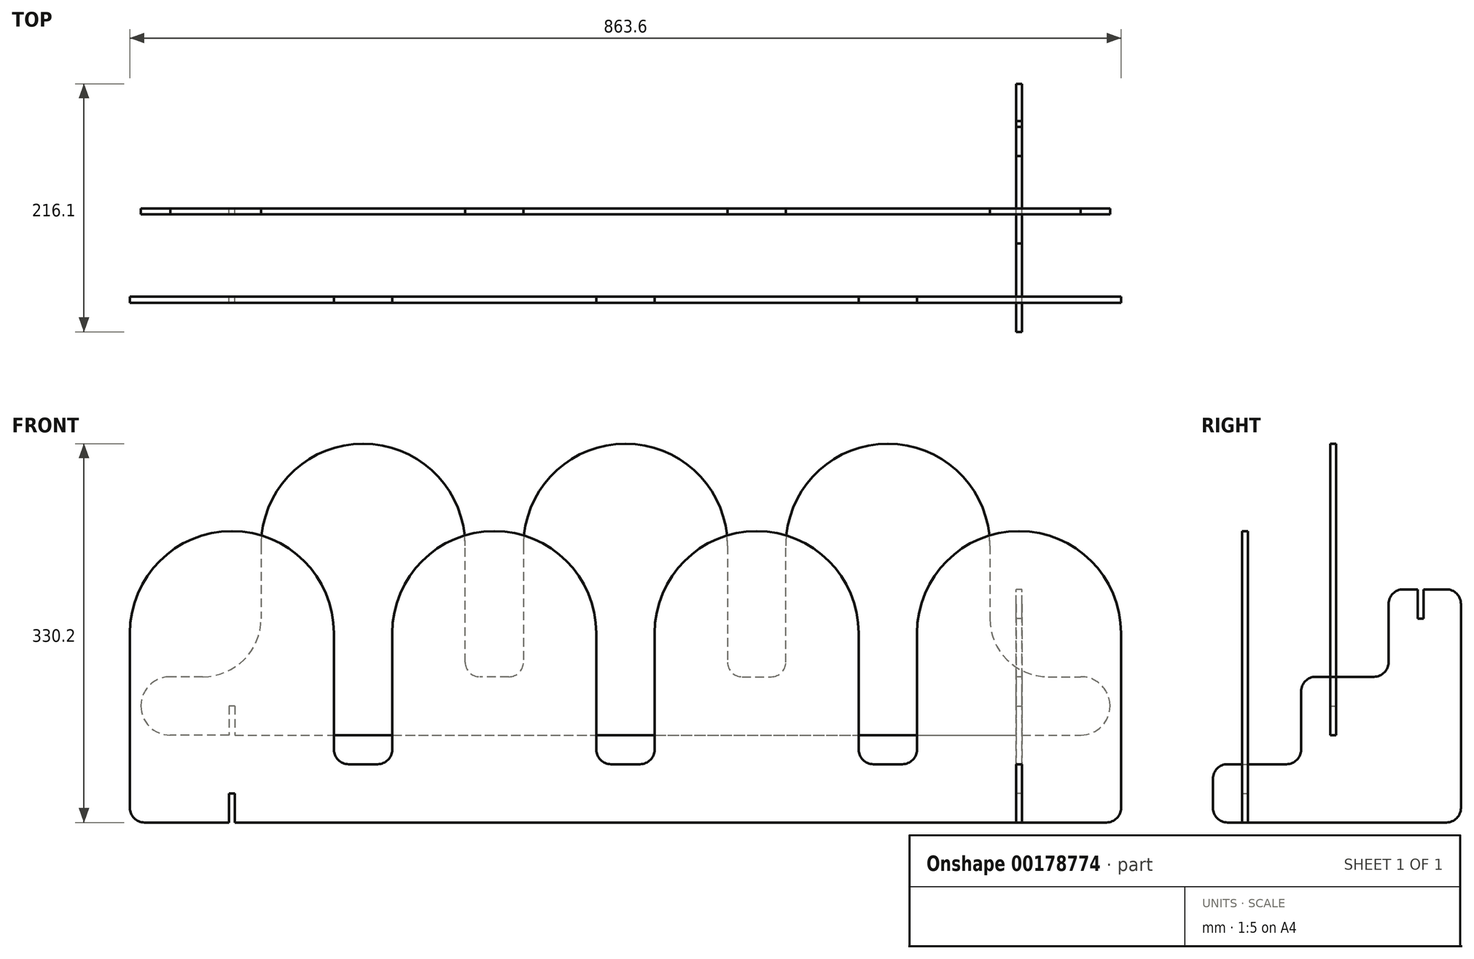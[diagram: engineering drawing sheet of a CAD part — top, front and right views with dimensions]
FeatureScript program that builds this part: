
annotation { "Feature Type Name" : "Feature", "Feature Type Description" : "" }
export const myFeature = defineFeature(function(context is Context, id is Id, definition is map)
    precondition{}
    {
        {
            var Q0;
            Q0=qCreatedBy(makeId("Front.planeOp"),FACE);
            var sketch = newSketch(context, id + "F0", { "sketchPlane" : qUnion([Q0])});
            skLineSegment(sketch, "E0", {"start": v(0, 0) * mm, "end": v(419.1, 0) * mm});
            skLineSegment(sketch, "E1", {"start": v(431.8, 12.7) * mm, "end": v(431.8, 165.1) * mm});
            skLineSegment(sketch, "E2", {"start": v(342.9, 254) * mm, "end": v(342.9, 254) * mm});
            skLineSegment(sketch, "E3", {"start": v(254, 165.1) * mm, "end": v(254, 63.5) * mm});
            skLineSegment(sketch, "E4", {"start": v(241.3, 50.8) * mm, "end": v(215.9, 50.8) * mm});
            skLineSegment(sketch, "E5", {"start": v(203.2, 63.5) * mm, "end": v(203.2, 165.1) * mm});
            skLineSegment(sketch, "E6", {"start": v(114.3, 254) * mm, "end": v(114.3, 254) * mm});
            skLineSegment(sketch, "E7", {"start": v(25.4, 165.1) * mm, "end": v(25.4, 63.5) * mm});
            skLineSegment(sketch, "E8", {"start": v(12.7, 50.8) * mm, "end": v(0, 50.8) * mm});
            skPoint(sketch, "E9.visualSharp", {"position": v(25.4, 254) * mm});
            skArc(sketch, "E9.filletArc", {"start": v(114.3, 254) * mm, "mid": v(51.44, 227.96) * mm, "end": v(25.4, 165.1) * mm});
            skPoint(sketch, "E10.visualSharp", {"position": v(203.2, 254) * mm});
            skArc(sketch, "E10.filletArc", {"start": v(203.2, 165.1) * mm, "mid": v(177.16, 227.96) * mm, "end": v(114.3, 254) * mm});
            skPoint(sketch, "E11.visualSharp", {"position": v(254, 254) * mm});
            skArc(sketch, "E11.filletArc", {"start": v(342.9, 254) * mm, "mid": v(280.04, 227.96) * mm, "end": v(254, 165.1) * mm});
            skPoint(sketch, "E12.visualSharp", {"position": v(431.8, 254) * mm});
            skArc(sketch, "E12.filletArc", {"start": v(431.8, 165.1) * mm, "mid": v(405.76, 227.96) * mm, "end": v(342.9, 254) * mm});
            skLineSegment(sketch, "E13.MirrorCS", {"start": v(-12.7, 50.8) * mm, "end": v(0, 50.8) * mm});
            skLineSegment(sketch, "E14.MirrorCS", {"start": v(0, 0) * mm, "end": v(-419.1, 0) * mm});
            skPoint(sketch, "E15.MirrorP", {"position": v(-25.4, 254) * mm});
            skPoint(sketch, "E16.MirrorP", {"position": v(-203.2, 254) * mm});
            skLineSegment(sketch, "E17.MirrorCS", {"start": v(-431.8, 12.7) * mm, "end": v(-431.8, 165.1) * mm});
            skLineSegment(sketch, "E18.MirrorCS", {"start": v(-254, 165.1) * mm, "end": v(-254, 63.5) * mm});
            skArc(sketch, "E19.MirrorCS", {"start": v(-203.2, 165.1) * mm, "mid": v(-177.16, 227.96) * mm, "end": v(-114.3, 254) * mm});
            skArc(sketch, "E20.MirrorCS", {"start": v(-342.9, 254) * mm, "mid": v(-280.04, 227.96) * mm, "end": v(-254, 165.1) * mm});
            skArc(sketch, "E21.MirrorCS", {"start": v(-431.8, 165.1) * mm, "mid": v(-405.76, 227.96) * mm, "end": v(-342.9, 254) * mm});
            skArc(sketch, "E22.MirrorCS", {"start": v(-114.3, 254) * mm, "mid": v(-51.44, 227.96) * mm, "end": v(-25.4, 165.1) * mm});
            skPoint(sketch, "E23.MirrorP", {"position": v(-431.8, 254) * mm});
            skPoint(sketch, "E24.MirrorP", {"position": v(-254, 254) * mm});
            skLineSegment(sketch, "E25.MirrorCS", {"start": v(-241.3, 50.8) * mm, "end": v(-215.9, 50.8) * mm});
            skLineSegment(sketch, "E26.MirrorCS", {"start": v(-203.2, 63.5) * mm, "end": v(-203.2, 165.1) * mm});
            skLineSegment(sketch, "E27.MirrorCS", {"start": v(-25.4, 165.1) * mm, "end": v(-25.4, 63.5) * mm});
            skLineSegment(sketch, "E28", {"start": v(-342.9, 165.1) * mm, "end": v(-342.9, 0) * mm, "construction": true});
            skLineSegment(sketch, "E29", {"start": v(-342.9, 25.4) * mm, "end": v(-340.28, 25.4) * mm});
            skLineSegment(sketch, "E30", {"start": v(-340.28, 25.4) * mm, "end": v(-340.28, 0) * mm});
            skLineSegment(sketch, "E31.MirrorCS", {"start": v(-345.52, 25.4) * mm, "end": v(-345.52, 0) * mm});
            skLineSegment(sketch, "E32.MirrorCS", {"start": v(-342.9, 25.4) * mm, "end": v(-345.52, 25.4) * mm});
            skLineSegment(sketch, "E33.MirrorCS", {"start": v(342.9, 25.4) * mm, "end": v(340.28, 25.4) * mm});
            skLineSegment(sketch, "E34.MirrorCS", {"start": v(342.9, 25.4) * mm, "end": v(345.52, 25.4) * mm});
            skLineSegment(sketch, "E35.MirrorCS", {"start": v(340.28, 25.4) * mm, "end": v(340.28, 0) * mm});
            skLineSegment(sketch, "E36.MirrorCS", {"start": v(345.52, 25.4) * mm, "end": v(345.52, 0) * mm});
            skPoint(sketch, "E37.visualSharp", {"position": v(-254, 50.8) * mm});
            skArc(sketch, "E37.filletArc", {"start": v(-254, 63.5) * mm, "mid": v(-250.28, 54.52) * mm, "end": v(-241.3, 50.8) * mm});
            skPoint(sketch, "E38.visualSharp", {"position": v(-203.2, 50.8) * mm});
            skArc(sketch, "E38.filletArc", {"start": v(-215.9, 50.8) * mm, "mid": v(-206.92, 54.52) * mm, "end": v(-203.2, 63.5) * mm});
            skPoint(sketch, "E39.visualSharp", {"position": v(-25.4, 50.8) * mm});
            skArc(sketch, "E39.filletArc", {"start": v(-25.4, 63.5) * mm, "mid": v(-21.68, 54.52) * mm, "end": v(-12.7, 50.8) * mm});
            skPoint(sketch, "E40.visualSharp", {"position": v(25.4, 50.8) * mm});
            skArc(sketch, "E40.filletArc", {"start": v(12.7, 50.8) * mm, "mid": v(21.68, 54.52) * mm, "end": v(25.4, 63.5) * mm});
            skPoint(sketch, "E41.visualSharp", {"position": v(-431.8, 0) * mm});
            skArc(sketch, "E41.filletArc", {"start": v(-431.8, 12.7) * mm, "mid": v(-428.08, 3.72) * mm, "end": v(-419.1, 0) * mm});
            skPoint(sketch, "E42.visualSharp", {"position": v(203.2, 50.8) * mm});
            skArc(sketch, "E42.filletArc", {"start": v(203.2, 63.5) * mm, "mid": v(206.92, 54.52) * mm, "end": v(215.9, 50.8) * mm});
            skPoint(sketch, "E43.visualSharp", {"position": v(254, 50.8) * mm});
            skArc(sketch, "E43.filletArc", {"start": v(241.3, 50.8) * mm, "mid": v(250.28, 54.52) * mm, "end": v(254, 63.5) * mm});
            skPoint(sketch, "E44.visualSharp", {"position": v(431.8, 0) * mm});
            skArc(sketch, "E44.filletArc", {"start": v(419.1, 0) * mm, "mid": v(428.08, 3.72) * mm, "end": v(431.8, 12.7) * mm});
            skSolve(sketch);
        }
        {
            var Q0;
            {var subQ4=sQuery(id+"F0.wireOp",EDGE,"E1");Q0=makeQuery(id+"F0.imprint","IMPRINT",FACE,{"disambiguationData":[TD([[makeQuery(id+"F0.imprint","IMPRINT",EDGE,{"derivedFrom":subQ4}),1.0]])]});}
            extrude(context, id + "F1", {"entities" : qUnion([Q0]), "depth" : 5.23 * mm});
        }
        {
            var Q0;
            Q0=makeQuery(id+"F1.opExtrude","SWEPT_FACE",FACE,{"disambiguationData":[OSD([sQuery(id+"F0.wireOp",EDGE,"E35.MirrorCS")])]});
            var sketch = newSketch(context, id + "F2", { "sketchPlane" : qUnion([Q0])});
            skLineSegment(sketch, "E45.0", {"start": v(-5.23, 25.4) * mm, "end": v(0, 25.4) * mm});
            skLineSegment(sketch, "E46", {"start": v(-30.63, 12.7) * mm, "end": v(-30.63, 38.1) * mm});
            skLineSegment(sketch, "E47", {"start": v(-17.93, 50.8) * mm, "end": v(-5.23, 50.8) * mm});
            skLineSegment(sketch, "E48", {"start": v(46.23, 63.5) * mm, "end": v(46.23, 114.3) * mm});
            skLineSegment(sketch, "E49", {"start": v(58.93, 127) * mm, "end": v(71.63, 127) * mm});
            skLineSegment(sketch, "E50", {"start": v(122.43, 139.7) * mm, "end": v(122.43, 190.5) * mm});
            skLineSegment(sketch, "E51", {"start": v(135.13, 203.2) * mm, "end": v(147.83, 203.2) * mm});
            skLineSegment(sketch, "E52", {"start": v(185.47, 190.5) * mm, "end": v(185.47, 12.7) * mm});
            skLineSegment(sketch, "E53", {"start": v(-5.23, 25.4) * mm, "end": v(-5.23, 50.8) * mm});
            skLineSegment(sketch, "E54", {"start": v(0, 25.4) * mm, "end": v(0, 50.8) * mm});
            skLineSegment(sketch, "E55.trimOffspring", {"start": v(0, 50.8) * mm, "end": v(33.53, 50.8) * mm});
            skLineSegment(sketch, "E56", {"start": v(71.63, 127) * mm, "end": v(71.63, 101.6) * mm});
            skLineSegment(sketch, "E57", {"start": v(71.63, 101.6) * mm, "end": v(76.86, 101.6) * mm});
            skLineSegment(sketch, "E58", {"start": v(76.86, 101.6) * mm, "end": v(76.86, 127) * mm});
            skLineSegment(sketch, "E59.trimOffspring", {"start": v(76.86, 127) * mm, "end": v(109.73, 127) * mm});
            skLineSegment(sketch, "E60", {"start": v(147.83, 203.2) * mm, "end": v(147.83, 177.8) * mm});
            skLineSegment(sketch, "E61", {"start": v(147.83, 177.8) * mm, "end": v(153.06, 177.8) * mm});
            skLineSegment(sketch, "E62", {"start": v(153.06, 177.8) * mm, "end": v(153.06, 203.2) * mm});
            skLineSegment(sketch, "E63.trimOffspring", {"start": v(153.06, 203.2) * mm, "end": v(172.77, 203.2) * mm});
            skLineSegment(sketch, "E64", {"start": v(-17.93, 0) * mm, "end": v(172.77, 0) * mm});
            skPoint(sketch, "E65.visualSharp", {"position": v(185.47, 0) * mm});
            skArc(sketch, "E65.filletArc", {"start": v(172.77, 0) * mm, "mid": v(181.75, 3.72) * mm, "end": v(185.47, 12.7) * mm});
            skPoint(sketch, "E66.visualSharp", {"position": v(185.47, 203.2) * mm});
            skArc(sketch, "E66.filletArc", {"start": v(185.47, 190.5) * mm, "mid": v(181.75, 199.48) * mm, "end": v(172.77, 203.2) * mm});
            skPoint(sketch, "E67.visualSharp", {"position": v(122.43, 203.2) * mm});
            skArc(sketch, "E67.filletArc", {"start": v(135.13, 203.2) * mm, "mid": v(126.15, 199.48) * mm, "end": v(122.43, 190.5) * mm});
            skPoint(sketch, "E68.visualSharp", {"position": v(122.43, 127) * mm});
            skArc(sketch, "E68.filletArc", {"start": v(109.73, 127) * mm, "mid": v(118.7, 130.72) * mm, "end": v(122.43, 139.7) * mm});
            skPoint(sketch, "E69.visualSharp", {"position": v(46.23, 127) * mm});
            skArc(sketch, "E69.filletArc", {"start": v(58.93, 127) * mm, "mid": v(49.95, 123.28) * mm, "end": v(46.23, 114.3) * mm});
            skPoint(sketch, "E70.visualSharp", {"position": v(46.23, 50.8) * mm});
            skArc(sketch, "E70.filletArc", {"start": v(33.53, 50.8) * mm, "mid": v(42.5, 54.52) * mm, "end": v(46.23, 63.5) * mm});
            skPoint(sketch, "E71.visualSharp", {"position": v(-30.63, 50.8) * mm});
            skArc(sketch, "E71.filletArc", {"start": v(-17.93, 50.8) * mm, "mid": v(-26.91, 47.08) * mm, "end": v(-30.63, 38.1) * mm});
            skPoint(sketch, "E72.visualSharp", {"position": v(-30.63, 0) * mm});
            skArc(sketch, "E72.filletArc", {"start": v(-30.63, 12.7) * mm, "mid": v(-26.91, 3.72) * mm, "end": v(-17.93, 0) * mm});
            skSolve(sketch);
        }
        {
            var Q0;
            Q0=makeQuery(id+"F2.imprint","IMPRINT",FACE,{"disambiguationData":[TD([[makeQuery(id+"F2.imprint","IMPRINT",EDGE,{"derivedFrom":sQuery(id+"F2.wireOp",EDGE,"E46")}),-1.0]])]});
            var Q1;
            Q1=makeQuery(id+"F2.imprint","IMPRINT",FACE,{"disambiguationData":[TD([[makeQuery(id+"F2.imprint","IMPRINT",EDGE,{"derivedFrom":sQuery(id+"F2.wireOp",EDGE,"E45.0")}),-1.0]])]});
            var Q2;
            Q2=makeQuery(id+"F2.imprint","IMPRINT",FACE,{"disambiguationData":[TD([[makeQuery(id+"F2.imprint","IMPRINT",EDGE,{"derivedFrom":sQuery(id+"F2.wireOp",EDGE,"E48")}),-1.0]])]});
            extrude(context, id + "F3", {"entities" : qUnion([Q0, Q1, Q2]), "depth" : 5.23 * mm});
        }
        {
            var Q0;
            Q0=makeQuery(id+"F3.opExtrude","SWEPT_FACE",FACE,{"disambiguationData":[OSD([sQuery(id+"F2.wireOp",EDGE,"E58")])]});
            var sketch = newSketch(context, id + "F4", { "sketchPlane" : qUnion([Q0])});
            skLineSegment(sketch, "E73", {"start": v(422.22, 76.2) * mm, "end": v(422.22, 76.2) * mm});
            skPoint(sketch, "E74.0", {"position": v(228.6, 50.8) * mm});
            skPoint(sketch, "E74.1", {"position": v(0, 50.8) * mm});
            skPoint(sketch, "E75.orphan", {"position": v(330.2, -228.6) * mm});
            skLineSegment(sketch, "E76", {"start": v(340.28, 76.2) * mm, "end": v(340.28, 50.8) * mm});
            skLineSegment(sketch, "E77", {"start": v(340.28, 50.8) * mm, "end": v(0, 50.8) * mm});
            skPoint(sketch, "E78.MirrorCS.end.orphan", {"position": v(-152.4, -182.88) * mm});
            skPoint(sketch, "E79.trimOffspring.end.orphan", {"position": v(127, -167.8) * mm});
            skPoint(sketch, "E79.trimOffspring.start.orphan", {"position": v(127.76, 50.8) * mm});
            skPoint(sketch, "E80.visualSharp", {"position": v(422.22, 101.6) * mm});
            skArc(sketch, "E80.filletArc", {"start": v(422.22, 76.2) * mm, "mid": v(414.7, 94.25) * mm, "end": v(396.57, 101.6) * mm});
            skPoint(sketch, "E81.visualSharp", {"position": v(422.22, 50.8) * mm});
            skArc(sketch, "E81.filletArc", {"start": v(396.82, 50.8) * mm, "mid": v(414.78, 58.24) * mm, "end": v(422.22, 76.2) * mm});
            skLineSegment(sketch, "E82", {"start": v(0, 304.8) * mm, "end": v(0, 304.8) * mm});
            skLineSegment(sketch, "E83", {"start": v(88.9, 215.9) * mm, "end": v(88.9, 114.3) * mm});
            skLineSegment(sketch, "E84", {"start": v(101.6, 101.6) * mm, "end": v(127, 101.6) * mm});
            skLineSegment(sketch, "E85", {"start": v(139.7, 114.3) * mm, "end": v(139.7, 215.9) * mm});
            skLineSegment(sketch, "E86", {"start": v(228.6, 304.8) * mm, "end": v(228.6, 304.8) * mm});
            skPoint(sketch, "E87.orphan", {"position": v(358.47, 304.8) * mm});
            skPoint(sketch, "E88.visualSharp", {"position": v(88.9, 304.8) * mm});
            skArc(sketch, "E88.filletArc", {"start": v(88.9, 215.9) * mm, "mid": v(62.86, 278.76) * mm, "end": v(0, 304.8) * mm});
            skPoint(sketch, "E89.visualSharp", {"position": v(88.9, 101.6) * mm});
            skArc(sketch, "E89.filletArc", {"start": v(88.9, 114.3) * mm, "mid": v(92.62, 105.32) * mm, "end": v(101.6, 101.6) * mm});
            skPoint(sketch, "E90.visualSharp", {"position": v(139.7, 101.6) * mm});
            skArc(sketch, "E90.filletArc", {"start": v(127, 101.6) * mm, "mid": v(135.98, 105.32) * mm, "end": v(139.7, 114.3) * mm});
            skPoint(sketch, "E91.visualSharp", {"position": v(317.5, 304.8) * mm});
            skArc(sketch, "E91.filletArc", {"start": v(317.5, 215.9) * mm, "mid": v(291.46, 278.76) * mm, "end": v(228.6, 304.8) * mm});
            skPoint(sketch, "E92.visualSharp", {"position": v(139.7, 304.8) * mm});
            skArc(sketch, "E92.filletArc", {"start": v(228.6, 304.8) * mm, "mid": v(165.74, 278.76) * mm, "end": v(139.7, 215.9) * mm});
            skPoint(sketch, "E93.start.orphan", {"position": v(345.52, 101.6) * mm});
            skLineSegment(sketch, "E94", {"start": v(317.5, 215.9) * mm, "end": v(317.5, 152.4) * mm});
            skLineSegment(sketch, "E95", {"start": v(368.3, 101.6) * mm, "end": v(396.57, 101.6) * mm});
            skPoint(sketch, "E96.visualSharp", {"position": v(317.5, 101.6) * mm});
            skArc(sketch, "E96.filletArc", {"start": v(317.5, 152.4) * mm, "mid": v(332.38, 116.48) * mm, "end": v(368.3, 101.6) * mm});
            skLineSegment(sketch, "E97.MirrorCS", {"start": v(-340.28, 76.2) * mm, "end": v(-340.28, 50.8) * mm});
            skLineSegment(sketch, "E98.MirrorCS", {"start": v(-368.3, 101.6) * mm, "end": v(-396.57, 101.6) * mm});
            skArc(sketch, "E99.MirrorCS", {"start": v(-127, 101.6) * mm, "mid": v(-135.98, 105.32) * mm, "end": v(-139.7, 114.3) * mm});
            skLineSegment(sketch, "E100.MirrorCS", {"start": v(-101.6, 101.6) * mm, "end": v(-127, 101.6) * mm});
            skArc(sketch, "E101.MirrorCS", {"start": v(-88.9, 114.3) * mm, "mid": v(-92.62, 105.32) * mm, "end": v(-101.6, 101.6) * mm});
            skArc(sketch, "E102.MirrorCS", {"start": v(-422.22, 76.2) * mm, "mid": v(-414.7, 94.25) * mm, "end": v(-396.57, 101.6) * mm});
            skArc(sketch, "E103.MirrorCS", {"start": v(-396.82, 50.8) * mm, "mid": v(-414.78, 58.24) * mm, "end": v(-422.22, 76.2) * mm});
            skPoint(sketch, "E104.MirrorP", {"position": v(-228.6, 50.8) * mm});
            skLineSegment(sketch, "E105.MirrorCS", {"start": v(-340.28, 50.8) * mm, "end": v(0, 50.8) * mm});
            skArc(sketch, "E106.MirrorCS", {"start": v(-88.9, 215.9) * mm, "mid": v(-62.86, 278.76) * mm, "end": v(0, 304.8) * mm});
            skLineSegment(sketch, "E107.MirrorCS", {"start": v(-88.9, 215.9) * mm, "end": v(-88.9, 114.3) * mm});
            skLineSegment(sketch, "E108.MirrorCS", {"start": v(-317.5, 215.9) * mm, "end": v(-317.5, 152.4) * mm});
            skPoint(sketch, "E109.MirrorP", {"position": v(-88.9, 304.8) * mm});
            skPoint(sketch, "E110.MirrorP", {"position": v(-317.5, 101.6) * mm});
            skPoint(sketch, "E111.MirrorP", {"position": v(-139.7, 304.8) * mm});
            skPoint(sketch, "E112.MirrorP", {"position": v(-358.47, 304.8) * mm});
            skPoint(sketch, "E113.MirrorP", {"position": v(-127.76, 50.8) * mm});
            skPoint(sketch, "E114.MirrorP", {"position": v(-317.5, 304.8) * mm});
            skArc(sketch, "E115.MirrorCS", {"start": v(-228.6, 304.8) * mm, "mid": v(-165.74, 278.76) * mm, "end": v(-139.7, 215.9) * mm});
            skPoint(sketch, "E116.MirrorP", {"position": v(-88.9, 101.6) * mm});
            skPoint(sketch, "E117.MirrorP", {"position": v(-422.22, 50.8) * mm});
            skPoint(sketch, "E118.MirrorP", {"position": v(-422.22, 101.6) * mm});
            skPoint(sketch, "E119.MirrorP", {"position": v(-139.7, 101.6) * mm});
            skLineSegment(sketch, "E120.MirrorCS", {"start": v(-228.6, 304.8) * mm, "end": v(-228.6, 304.8) * mm});
            skPoint(sketch, "E121.MirrorP", {"position": v(-345.52, 101.6) * mm});
            skArc(sketch, "E122.MirrorCS", {"start": v(-317.5, 152.4) * mm, "mid": v(-332.38, 116.48) * mm, "end": v(-368.3, 101.6) * mm});
            skLineSegment(sketch, "E123.MirrorCS", {"start": v(-422.22, 76.2) * mm, "end": v(-422.22, 76.2) * mm});
            skLineSegment(sketch, "E124.MirrorCS", {"start": v(-139.7, 114.3) * mm, "end": v(-139.7, 215.9) * mm});
            skArc(sketch, "E125.MirrorCS", {"start": v(-317.5, 215.9) * mm, "mid": v(-291.46, 278.76) * mm, "end": v(-228.6, 304.8) * mm});
            skPoint(sketch, "E126.MirrorCS.end.orphan", {"position": v(-358.47, 76.2) * mm});
            skPoint(sketch, "E127.MirrorCS.start.orphan", {"position": v(-371.42, 50.8) * mm});
            skLineSegment(sketch, "E128.MirrorCS", {"start": v(-345.52, 76.2) * mm, "end": v(-345.52, 50.8) * mm});
            skLineSegment(sketch, "E129", {"start": v(-340.28, 76.2) * mm, "end": v(-345.52, 76.2) * mm});
            skLineSegment(sketch, "E130", {"start": v(-371.42, 50.8) * mm, "end": v(-396.82, 50.8) * mm});
            skPoint(sketch, "E131.start.orphan", {"position": v(358.47, 76.2) * mm});
            skPoint(sketch, "E132.start.orphan", {"position": v(371.42, 50.8) * mm});
            skLineSegment(sketch, "E133", {"start": v(340.28, 76.2) * mm, "end": v(345.52, 76.2) * mm});
            skLineSegment(sketch, "E134", {"start": v(345.52, 76.2) * mm, "end": v(345.52, 50.8) * mm});
            skLineSegment(sketch, "E135", {"start": v(345.52, 50.8) * mm, "end": v(396.82, 50.8) * mm});
            skLineSegment(sketch, "E136", {"start": v(-371.42, 50.8) * mm, "end": v(-345.52, 50.8) * mm});
            skSolve(sketch);
        }
        {
            var Q0;
            {var subQ1=sQuery(id+"F2.wireOp",EDGE,"E58");var subQ6=makeQuery(id+"F3.opExtrude","SWEPT_EDGE",EDGE,{"disambiguationData":[OSD([sQuery(id+"F2.wireOp",EDGE,"E57"),subQ1])]});Q0=makeQuery(id+"F4.imprint","IMPRINT",FACE,{"disambiguationData":[TD([[makeQuery(id+"F4.imprint","IMPRINT",EDGE,{"derivedFrom":subQ6}),-1.0]])]});}
            var Q1;
            Q1=makeQuery(id+"F4.imprint","IMPRINT",FACE,{"disambiguationData":[TD([[makeQuery(id+"F4.imprint","IMPRINT",EDGE,{"derivedFrom":sQuery(id+"F4.wireOp",EDGE,"E73")}),1.0]])]});
            extrude(context, id + "F5", {"entities" : qUnion([Q0, Q1]), "depth" : 5.23 * mm});
        }
        {
            var Q0;
            Q0=makeQuery(id+"F5.opExtrude","SWEPT_BODY",BODY,{"disambiguationData":[OSD([sQuery(id+"F2.wireOp",EDGE,"E57"),sQuery(id+"F2.wireOp",EDGE,"E58"),sQuery(id+"F4.wireOp",EDGE,"E131"),sQuery(id+"F4.wireOp",EDGE,"E132"),sQuery(id+"F4.wireOp",EDGE,"F4H2BkGv-ek3y-bC0f-7BX3-DHjXtJ8XUS1k.left"),sQuery(id+"F4.wireOp",EDGE,"F4H2BkGv-ek3y-bC0f-7BX3-DHjXtJ8XUS1k.right"),sQuery(id+"F4.wireOp",EDGE,"Ar85Rdxf-3x7w-sshh-eHF4-fIjZdYVxne9i"),sQuery(id+"F4.wireOp",EDGE,"pdUOoqc8-6pFK-XO5Y-qC8V-1omtSayrR1Eh"),sQuery(id+"F4.wireOp",EDGE,"E76"),sQuery(id+"F4.wireOp",EDGE,"E77"),sQuery(id+"F4.wireOp",EDGE,"769f3142-1af8-4ec9-886a-1fccbde9820d3.MirrorCS"),sQuery(id+"F4.wireOp",EDGE,"769f3142-1af8-4ec9-886a-1fccbde9820d5.MirrorCS"),sQuery(id+"F4.wireOp",EDGE,"769f3142-1af8-4ec9-886a-1fccbde9820d7.MirrorCS"),sQuery(id+"F4.wireOp",EDGE,"769f3142-1af8-4ec9-886a-1fccbde9820d11.MirrorCS"),sQuery(id+"F4.wireOp",EDGE,"769f3142-1af8-4ec9-886a-1fccbde9820d12.MirrorCS"),sQuery(id+"F4.wireOp",EDGE,"769f3142-1af8-4ec9-886a-1fccbde9820d13.MirrorCS"),sQuery(id+"F4.wireOp",EDGE,"769f3142-1af8-4ec9-886a-1fccbde9820d14.MirrorCS"),sQuery(id+"F4.wireOp",EDGE,"769f3142-1af8-4ec9-886a-1fccbde9820d16.MirrorCS"),sQuery(id+"F4.wireOp",EDGE,"769f3142-1af8-4ec9-886a-1fccbde9820d17.MirrorCS"),sQuery(id+"F4.wireOp",EDGE,"3e02c22d-247e-4edf-9cdd-5e5ad40c3efc.filletArc"),sQuery(id+"F4.wireOp",EDGE,"0cda2c84-7136-4183-a7d9-16cdea820c9e.filletArc"),sQuery(id+"F4.wireOp",EDGE,"1b53a4fb-0f16-46a5-bf37-dce67859a060.filletArc"),sQuery(id+"F4.wireOp",EDGE,"99aa08da-a2c4-4532-bf4b-e225fbfdf051.filletArc"),sQuery(id+"F4.wireOp",EDGE,"a2c9f93e-e2b4-4357-ae06-c20cbb8bdb9b.filletArc"),sQuery(id+"F4.wireOp",EDGE,"41861de6-56c0-405a-a797-85e97318e828.filletArc"),sQuery(id+"F4.wireOp",EDGE,"fe7535a8-a8be-412e-99f0-801e2ade721e.filletArc"),sQuery(id+"F4.wireOp",EDGE,"a99daf98-5c19-4628-9276-8528c6106e63.filletArc"),sQuery(id+"F4.wireOp",EDGE,"358fcf2a-b2dd-4258-8af7-4781002b3bd8.filletArc"),sQuery(id+"F4.wireOp",EDGE,"cfa27c8a-caf5-4cee-a6ec-8dcada9c895b.filletArc"),sQuery(id+"F4.wireOp",EDGE,"531d461e-7225-4e4c-9478-6120f39ccf02.filletArc"),sQuery(id+"F4.wireOp",EDGE,"E80.filletArc"),sQuery(id+"F4.wireOp",EDGE,"E81.filletArc"),sQuery(id+"F4.wireOp",EDGE,"c4f2a757-1e52-46f9-abde-accc6e027c3c.filletArc"),sQuery(id+"F4.wireOp",EDGE,"55916f88-8188-49cb-9c31-3b824ec4ddf0.filletArc"),sQuery(id+"F4.wireOp",EDGE,"LfmB6QBN-igk6-ITNq-QIwP-ZOp6VIhb9ITS"),sQuery(id+"F4.wireOp",EDGE,"1vKX9kf7-W4JJ-SDBf-ucQd-GPJkoue8bs8R"),sQuery(id+"F4.wireOp",EDGE,"6vQfJ0yM-COM2-AVFx-pEkk-nLMdVWfa1WtS"),sQuery(id+"F4.wireOp",EDGE,"32cb3646-9896-40d9-916f-fccc941b47d1.filletArc")])]});
            transform(context, id + "F6", {"entities" : qUnion([Q0]), "transformType" : TransformType.TRANSLATION_3D, "dx" : 0 * mm, "dy" : 0 * mm, "dz" : 25.4 * mm, "makeCopy" : false});
        }
    });
